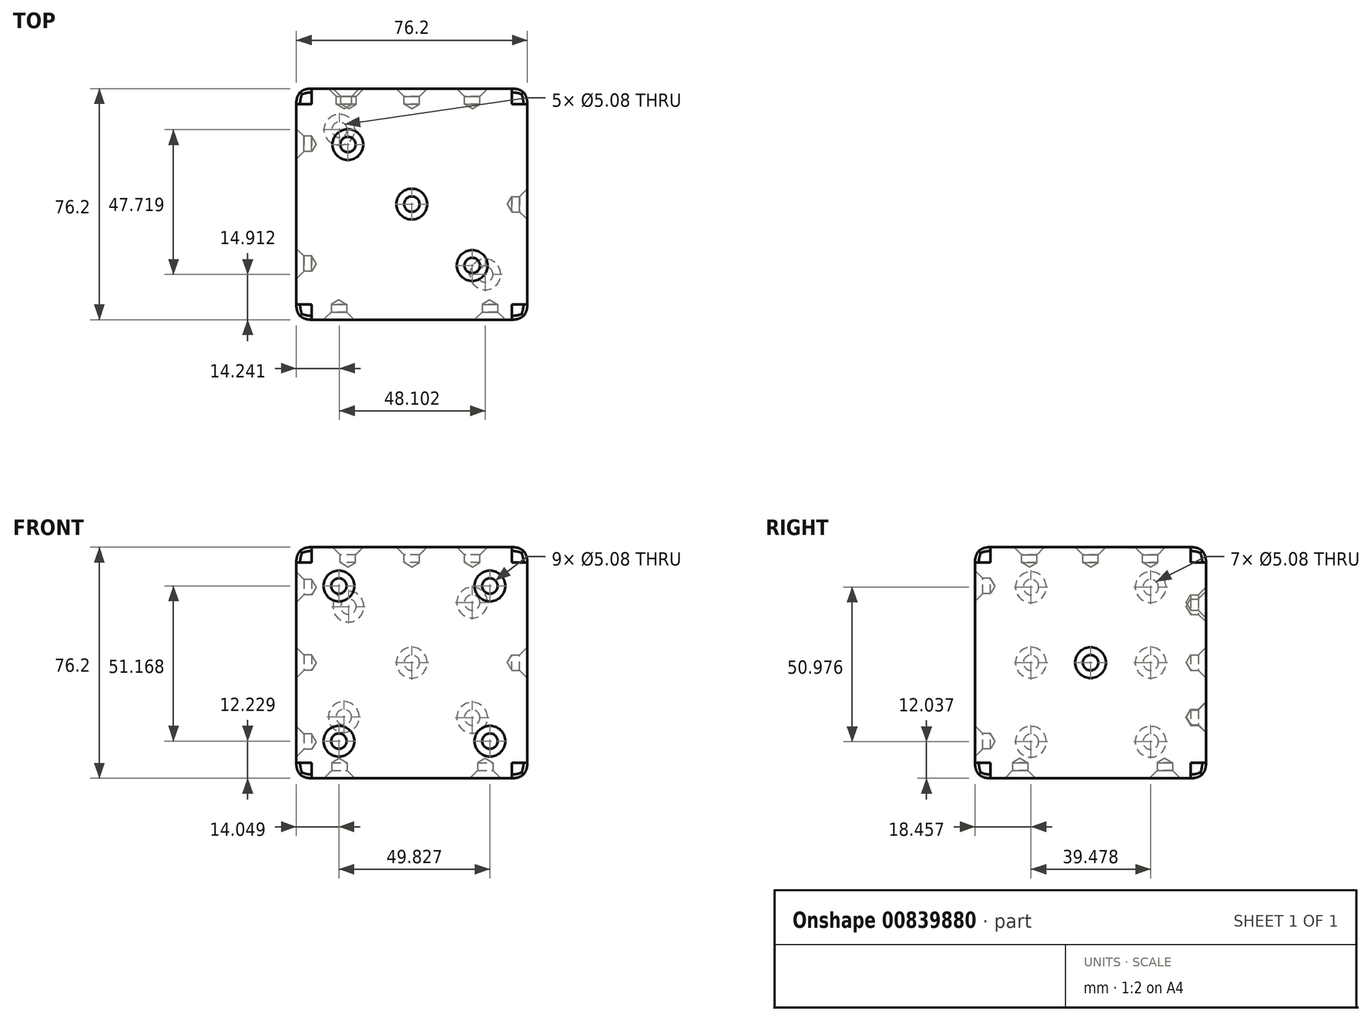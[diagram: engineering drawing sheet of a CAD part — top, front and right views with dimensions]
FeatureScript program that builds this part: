
annotation { "Feature Type Name" : "Feature", "Feature Type Description" : "" }
export const myFeature = defineFeature(function(context is Context, id is Id, definition is map)
    precondition{}
    {
        {
            var Q0;
            Q0=qCreatedBy(makeId("Front.planeOp"),FACE);
            var sketch = newSketch(context, id + "F0", { "sketchPlane" : qUnion([Q0])});
            skLineSegment(sketch, "E0.bottom", {"start": v(38.1, -38.1) * mm, "end": v(-38.1, -38.1) * mm});
            skLineSegment(sketch, "E0.top", {"start": v(38.1, 38.1) * mm, "end": v(-38.1, 38.1) * mm});
            skLineSegment(sketch, "E0.left", {"start": v(38.1, -38.1) * mm, "end": v(38.1, 38.1) * mm});
            skLineSegment(sketch, "E0.right", {"start": v(-38.1, -38.1) * mm, "end": v(-38.1, 38.1) * mm});
            skPoint(sketch, "E0.middle", {"position": v(0, 0) * mm});
            skSolve(sketch);
        }
        {
            var Q0;
            Q0=makeQuery(id+"F0.imprint","IMPRINT",FACE,{"disambiguationData":[TD([[makeQuery(id+"F0.imprint","IMPRINT",EDGE,{"derivedFrom":sQuery(id+"F0.wireOp",EDGE,"E0.bottom")}),-1.0]])]});
            extrude(context, id + "F1", {"entities" : qUnion([Q0]), "endBound" : BoundingType.SYMMETRIC, "depth" : 76.2 * mm, "offsetDistance" : 25.4 * mm});
        }
        {
            var Q0;
            Q0=makeQuery(id+"F1.opExtrude","SWEPT_FACE",FACE,{"disambiguationData":[OSD([sQuery(id+"F0.wireOp",EDGE,"E0.top")])]});
            var Q1;
            Q1=makeQuery(id+"F1.opExtrude","SWEPT_FACE",FACE,{"disambiguationData":[OSD([sQuery(id+"F0.wireOp",EDGE,"E0.right")])]});
            var Q2;
            Q2=makeQuery(id+"F1.opExtrude","CAP_FACE",FACE,{"disambiguationData":[OSD([sQuery(id+"F0.wireOp",EDGE,"E0.bottom"),sQuery(id+"F0.wireOp",EDGE,"E0.top"),sQuery(id+"F0.wireOp",EDGE,"E0.left"),sQuery(id+"F0.wireOp",EDGE,"E0.right")])],"isStart":false});
            var Q3;
            Q3=makeQuery(id+"F1.opExtrude","SWEPT_FACE",FACE,{"disambiguationData":[OSD([sQuery(id+"F0.wireOp",EDGE,"E0.bottom")])]});
            var Q4;
            Q4=makeQuery(id+"F1.opExtrude","CAP_FACE",FACE,{"disambiguationData":[OSD([sQuery(id+"F0.wireOp",EDGE,"E0.bottom"),sQuery(id+"F0.wireOp",EDGE,"E0.top"),sQuery(id+"F0.wireOp",EDGE,"E0.left"),sQuery(id+"F0.wireOp",EDGE,"E0.right")])],"isStart":true});
            var Q5;
            Q5=makeQuery(id+"F1.opExtrude","SWEPT_FACE",FACE,{"disambiguationData":[OSD([sQuery(id+"F0.wireOp",EDGE,"E0.left")])]});
            fillet(context, id + "F2", {"entities" : qUnion([Q0, Q1, Q2, Q3, Q4, Q5]), "radius" : 5.08 * mm, "tangentPropagation" : true, "rho" : .5, "crossSection" : FilletCrossSection.CONIC, "allowEdgeOverflow" : false});
        }
        {
            var Q0;
            Q0=makeQuery(id+"F1.opExtrude","CAP_FACE",FACE,{"disambiguationData":[OSD([sQuery(id+"F0.wireOp",EDGE,"E0.bottom"),sQuery(id+"F0.wireOp",EDGE,"E0.top"),sQuery(id+"F0.wireOp",EDGE,"E0.left"),sQuery(id+"F0.wireOp",EDGE,"E0.right")])],"isStart":false});
            var sketch = newSketch(context, id + "F3", { "sketchPlane" : qUnion([Q0])});
            skPoint(sketch, "E1", {"position": v(-24.05, 25.3) * mm});
            skPoint(sketch, "E2", {"position": v(25.78, 25.3) * mm});
            skPoint(sketch, "E3", {"position": v(25.78, -25.87) * mm});
            skPoint(sketch, "E4", {"position": v(-24.05, -25.87) * mm});
            skSolve(sketch);
        }
        {
            var Q0;
            Q0=sQuery(id+"F3.wireOp",VERTEX,"E1");
            var Q1;
            Q1=sQuery(id+"F3.wireOp",VERTEX,"E2");
            var Q2;
            Q2=sQuery(id+"F3.wireOp",VERTEX,"E3");
            var Q3;
            Q3=sQuery(id+"F3.wireOp",VERTEX,"E4");
            var Q4;
            Q4=makeQuery(id+"F1.opExtrude","SWEPT_BODY",BODY,{"disambiguationData":[OSD([sQuery(id+"F0.wireOp",EDGE,"E0.bottom"),sQuery(id+"F0.wireOp",EDGE,"E0.top"),sQuery(id+"F0.wireOp",EDGE,"E0.left"),sQuery(id+"F0.wireOp",EDGE,"E0.right")])]});
            hole(context, id + "F4", {"style" : HoleStyle.C_SINK, "endStyle" : HoleEndStyle.BLIND, "holeDiameter" : 5.08 * mm, "cSinkDiameter" : 10.16 * mm, "cSinkAngle" : 90 * degree, "majorDiameter" : 6.35 * mm, "holeDepth" : 5.08 * mm, "isTappedThrough" : true, "tappedDepth" : 12.7 * mm, "tapClearance" : 3, "locations" : qUnion([Q0, Q1, Q2, Q3]), "scope" : qUnion([Q4])});
        }
        {
            var Q0;
            Q0=makeQuery(id+"F1.opExtrude","SWEPT_FACE",FACE,{"disambiguationData":[OSD([sQuery(id+"F0.wireOp",EDGE,"E0.bottom")])]});
            var sketch = newSketch(context, id + "F5", { "sketchPlane" : qUnion([Q0])});
            skPoint(sketch, "E5", {"position": v(-23.86, -24.53) * mm});
            skPoint(sketch, "E6", {"position": v(24.24, 23.19) * mm});
            skSolve(sketch);
        }
        {
            var Q0;
            Q0=sQuery(id+"F5.wireOp",VERTEX,"E5");
            var Q1;
            Q1=sQuery(id+"F5.wireOp",VERTEX,"E6");
            var Q2;
            Q2=makeQuery(id+"F1.opExtrude","SWEPT_BODY",BODY,{"disambiguationData":[OSD([sQuery(id+"F0.wireOp",EDGE,"E0.bottom"),sQuery(id+"F0.wireOp",EDGE,"E0.top"),sQuery(id+"F0.wireOp",EDGE,"E0.left"),sQuery(id+"F0.wireOp",EDGE,"E0.right")])]});
            hole(context, id + "F6", {"style" : HoleStyle.C_SINK, "endStyle" : HoleEndStyle.BLIND, "holeDiameter" : 5.08 * mm, "cSinkDiameter" : 10.16 * mm, "cSinkAngle" : 90 * degree, "majorDiameter" : 6.35 * mm, "holeDepth" : 5.08 * mm, "isTappedThrough" : true, "tappedDepth" : 12.7 * mm, "tapClearance" : 3, "locations" : qUnion([Q0, Q1]), "scope" : qUnion([Q2])});
        }
        {
            var Q0;
            Q0=makeQuery(id+"F1.opExtrude","SWEPT_FACE",FACE,{"disambiguationData":[OSD([sQuery(id+"F0.wireOp",EDGE,"E0.left")])]});
            var sketch = newSketch(context, id + "F7", { "sketchPlane" : qUnion([Q0])});
            skPoint(sketch, "E7", {"position": v(0, 0) * mm});
            skSolve(sketch);
        }
        {
            var Q0;
            Q0=sQuery(id+"F7.wireOp",VERTEX,"E7");
            var Q1;
            Q1=makeQuery(id+"F1.opExtrude","SWEPT_BODY",BODY,{"disambiguationData":[OSD([sQuery(id+"F0.wireOp",EDGE,"E0.bottom"),sQuery(id+"F0.wireOp",EDGE,"E0.top"),sQuery(id+"F0.wireOp",EDGE,"E0.left"),sQuery(id+"F0.wireOp",EDGE,"E0.right")])]});
            hole(context, id + "F8", {"style" : HoleStyle.C_SINK, "endStyle" : HoleEndStyle.BLIND, "holeDiameter" : 5.08 * mm, "cSinkDiameter" : 10.16 * mm, "cSinkAngle" : 90 * degree, "majorDiameter" : 6.35 * mm, "holeDepth" : 5.08 * mm, "isTappedThrough" : true, "tappedDepth" : 12.7 * mm, "tapClearance" : 3, "locations" : qUnion([Q0]), "scope" : qUnion([Q1])});
        }
        {
            var Q0;
            Q0=makeQuery(id+"F1.opExtrude","SWEPT_FACE",FACE,{"disambiguationData":[OSD([sQuery(id+"F0.wireOp",EDGE,"E0.right")])]});
            var sketch = newSketch(context, id + "F9", { "sketchPlane" : qUnion([Q0])});
            skPoint(sketch, "E8", {"position": v(-19.83, 24.91) * mm});
            skPoint(sketch, "E9", {"position": v(-19.83, 0) * mm});
            skPoint(sketch, "E10", {"position": v(-19.83, -26.06) * mm});
            skPoint(sketch, "E11", {"position": v(19.64, -26.06) * mm});
            skPoint(sketch, "E12", {"position": v(19.64, 0) * mm});
            skPoint(sketch, "E13", {"position": v(19.64, 24.91) * mm});
            skSolve(sketch);
        }
        {
            var Q0;
            Q0=sQuery(id+"F9.wireOp",VERTEX,"E8");
            var Q1;
            Q1=sQuery(id+"F9.wireOp",VERTEX,"E9");
            var Q2;
            Q2=sQuery(id+"F9.wireOp",VERTEX,"E10");
            var Q3;
            Q3=sQuery(id+"F9.wireOp",VERTEX,"E13");
            var Q4;
            Q4=sQuery(id+"F9.wireOp",VERTEX,"E12");
            var Q5;
            Q5=sQuery(id+"F9.wireOp",VERTEX,"E11");
            var Q6;
            Q6=makeQuery(id+"F1.opExtrude","SWEPT_BODY",BODY,{"disambiguationData":[OSD([sQuery(id+"F0.wireOp",EDGE,"E0.bottom"),sQuery(id+"F0.wireOp",EDGE,"E0.top"),sQuery(id+"F0.wireOp",EDGE,"E0.left"),sQuery(id+"F0.wireOp",EDGE,"E0.right")])]});
            hole(context, id + "F10", {"style" : HoleStyle.C_SINK, "endStyle" : HoleEndStyle.BLIND, "holeDiameter" : 5.08 * mm, "cSinkDiameter" : 10.16 * mm, "cSinkAngle" : 90 * degree, "majorDiameter" : 6.35 * mm, "holeDepth" : 5.08 * mm, "isTappedThrough" : true, "tappedDepth" : 12.7 * mm, "tapClearance" : 3, "locations" : qUnion([Q0, Q1, Q2, Q3, Q4, Q5]), "scope" : qUnion([Q6])});
        }
        {
            var Q0;
            Q0=makeQuery(id+"F1.opExtrude","SWEPT_FACE",FACE,{"disambiguationData":[OSD([sQuery(id+"F0.wireOp",EDGE,"E0.top")])]});
            var sketch = newSketch(context, id + "F11", { "sketchPlane" : qUnion([Q0])});
            skPoint(sketch, "E14", {"position": v(19.93, -20.22) * mm});
            skPoint(sketch, "E15", {"position": v(0, 0) * mm});
            skPoint(sketch, "E16", {"position": v(-21.08, 19.64) * mm});
            skSolve(sketch);
        }
        {
            var Q0;
            Q0=sQuery(id+"F11.wireOp",VERTEX,"E14");
            var Q1;
            Q1=sQuery(id+"F11.wireOp",VERTEX,"E15");
            var Q2;
            Q2=sQuery(id+"F11.wireOp",VERTEX,"E16");
            var Q3;
            Q3=makeQuery(id+"F1.opExtrude","SWEPT_BODY",BODY,{"disambiguationData":[OSD([sQuery(id+"F0.wireOp",EDGE,"E0.bottom"),sQuery(id+"F0.wireOp",EDGE,"E0.top"),sQuery(id+"F0.wireOp",EDGE,"E0.left"),sQuery(id+"F0.wireOp",EDGE,"E0.right")])]});
            hole(context, id + "F12", {"style" : HoleStyle.C_SINK, "endStyle" : HoleEndStyle.BLIND, "holeDiameter" : 5.08 * mm, "cSinkDiameter" : 10.16 * mm, "cSinkAngle" : 90 * degree, "majorDiameter" : 6.35 * mm, "holeDepth" : 5.08 * mm, "isTappedThrough" : true, "tappedDepth" : 12.7 * mm, "tapClearance" : 3, "locations" : qUnion([Q0, Q1, Q2]), "scope" : qUnion([Q3])});
        }
        {
            var Q0;
            Q0=makeQuery(id+"F1.opExtrude","CAP_FACE",FACE,{"disambiguationData":[OSD([sQuery(id+"F0.wireOp",EDGE,"E0.bottom"),sQuery(id+"F0.wireOp",EDGE,"E0.top"),sQuery(id+"F0.wireOp",EDGE,"E0.left"),sQuery(id+"F0.wireOp",EDGE,"E0.right")])],"isStart":true});
            var sketch = newSketch(context, id + "F13", { "sketchPlane" : qUnion([Q0])});
            skPoint(sketch, "E17", {"position": v(20.89, 18.5) * mm});
            skPoint(sketch, "E18", {"position": v(22.42, -17.92) * mm});
            skPoint(sketch, "E19", {"position": v(-19.93, -18.11) * mm});
            skPoint(sketch, "E20", {"position": v(-19.93, 19.83) * mm});
            skPoint(sketch, "E21", {"position": v(0, 0) * mm});
            skSolve(sketch);
        }
        {
            var Q0;
            Q0=sQuery(id+"F13.wireOp",VERTEX,"E17");
            var Q1;
            Q1=sQuery(id+"F13.wireOp",VERTEX,"E18");
            var Q2;
            Q2=sQuery(id+"F13.wireOp",VERTEX,"E21");
            var Q3;
            Q3=sQuery(id+"F13.wireOp",VERTEX,"E19");
            var Q4;
            Q4=sQuery(id+"F13.wireOp",VERTEX,"E20");
            var Q5;
            Q5=makeQuery(id+"F1.opExtrude","SWEPT_BODY",BODY,{"disambiguationData":[OSD([sQuery(id+"F0.wireOp",EDGE,"E0.bottom"),sQuery(id+"F0.wireOp",EDGE,"E0.top"),sQuery(id+"F0.wireOp",EDGE,"E0.left"),sQuery(id+"F0.wireOp",EDGE,"E0.right")])]});
            hole(context, id + "F14", {"style" : HoleStyle.C_SINK, "endStyle" : HoleEndStyle.BLIND, "holeDiameter" : 5.08 * mm, "cSinkDiameter" : 10.16 * mm, "cSinkAngle" : 90 * degree, "majorDiameter" : 6.35 * mm, "holeDepth" : 5.08 * mm, "isTappedThrough" : true, "tappedDepth" : 12.7 * mm, "tapClearance" : 3, "locations" : qUnion([Q0, Q1, Q2, Q3, Q4]), "scope" : qUnion([Q5])});
        }
        {
            var Q0;
            Q0=makeQuery(id+"F1.opExtrude","SWEPT_BODY",BODY,{"disambiguationData":[OSD([sQuery(id+"F0.wireOp",EDGE,"E0.bottom"),sQuery(id+"F0.wireOp",EDGE,"E0.top"),sQuery(id+"F0.wireOp",EDGE,"E0.left"),sQuery(id+"F0.wireOp",EDGE,"E0.right")])]});
            transform(context, id + "F15", {"entities" : qUnion([Q0]), "transformType" : TransformType.TRANSLATION_3D, "dx" : 0 * mm, "dy" : 0 * mm, "dz" : 0 * mm, "makeCopy" : true});
        }
        {
            var Q0;
            Q0=makeQuery(id+"F15.opPattern","COPY",BODY,{"derivedFrom":makeQuery(id+"F1.opExtrude","SWEPT_BODY",BODY,{"disambiguationData":[OSD([sQuery(id+"F0.wireOp",EDGE,"E0.bottom"),sQuery(id+"F0.wireOp",EDGE,"E0.top"),sQuery(id+"F0.wireOp",EDGE,"E0.left"),sQuery(id+"F0.wireOp",EDGE,"E0.right")])]}),"instanceName":"1"});
            deleteBodies(context, id + "F16", {"entities" : qUnion([Q0])});
        }
    });
